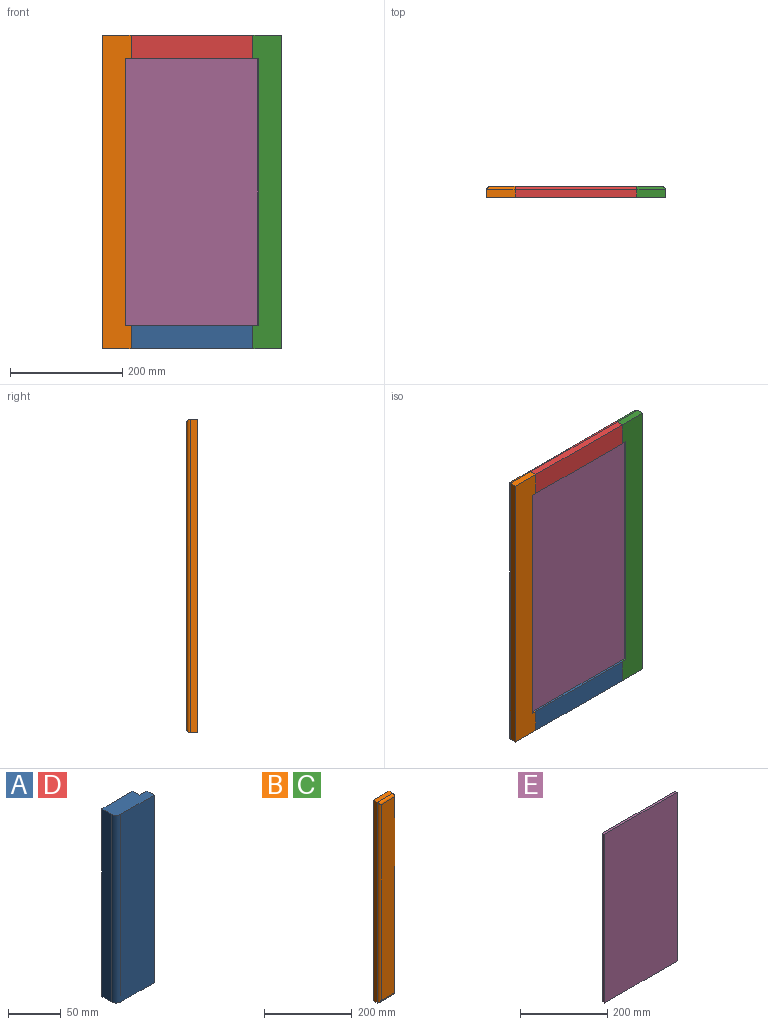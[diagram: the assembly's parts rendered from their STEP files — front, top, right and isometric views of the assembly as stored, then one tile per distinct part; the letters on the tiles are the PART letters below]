
ASSEMBLY  parts=5 mates=4
PART A: 9 faces, bbox 50.8x19.1x217.5 mm
  f0: plane 50.8x19.05mm, normal (0,0,1), area 868.4mm2, adj f2,f3,f4,f5,f6,f7,f8
  f1: plane 50.8x19.05mm, normal (0,0,-1), area 868.4mm2, adj f2,f3,f4,f5,f6,f7,f8
  f2: plane 217.49x12.7mm, normal (-1,0,0), area 2762.1mm2, adj f0,f1,f5,f6
  f3: plane 217.49x44.45mm, normal (0,-1,0), area 9667.3mm2, adj f0,f1,f4,f6
  f4: plane 217.49x9.53mm, normal (1,0,0), area 2071.6mm2, adj f0,f1,f3,f7
  f5: plane 217.49x41.28mm, normal (0,1,0), area 8976.8mm2, adj f0,f1,f2,f8
  f6: cylinder r=6.35mm len=217.49mm, axis (0,0,1), area 2169.3mm2, adj f0,f1,f2,f3
  f7: plane 217.49x9.53mm, normal (0,1,0), area 2071.6mm2, adj f0,f1,f4,f8
  f8: plane 217.49x9.53mm, normal (1,0,0), area 2071.6mm2, adj f0,f1,f5,f7
PART B: 13 faces, bbox 50.8x19.1x558.8 mm
  f0: plane 558.8x19.05mm, normal (1,0,0), area 6091.6mm2, adj f1,f3,f4,f5,f6,f7,f9,f10
  f1: plane 558.8x50.8mm, normal (0,1,0), area 23850.8mm2, adj f0,f2,f4,f5,f9,f10,f11
  f2: plane 558.8x12.7mm, normal (-1,0,0), area 7096.8mm2, adj f1,f4,f5,f8
  f3: plane 546.1x44.45mm, normal (0,-1,0), area 24274.1mm2, adj f0,f6,f7,f8
  f4: plane 50.8x12.7mm, normal (0,0,1), area 645.2mm2, adj f0,f1,f2,f6
  f5: plane 50.8x12.7mm, normal (0,0,-1), area 645.2mm2, adj f0,f1,f2,f7
  f6: cylinder r=6.35mm len=50.8mm, axis (-1,0,0), area 483.7mm2, adj f0,f3,f4,f8
  f7: cylinder r=6.35mm len=50.8mm, axis (1,0,0), area 483.7mm2, adj f0,f3,f5,f8
  f8: cylinder r=6.35mm len=558.8mm, axis (0,0,1), area 5527.8mm2, adj f2,f3,f6,f7
  f9: plane 9.53x9.53mm, normal (0,0,1), area 90.7mm2, adj f0,f1,f11,f12
  f10: plane 9.53x9.53mm, normal (0,0,-1), area 90.7mm2, adj f0,f1,f11,f12
  f11: plane 476.25x9.53mm, normal (1,0,0), area 4536.3mm2, adj f1,f9,f10,f12
  f12: plane 476.25x9.53mm, normal (0,1,0), area 4536.3mm2, adj f0,f9,f10,f11
PART C: same geometry as B
PART D: same geometry as A
PART E: 6 faces, bbox 236.5x6.4x474.7 mm
  f0: plane 474.66x6.35mm, normal (-1,0,0), area 3014.1mm2, adj f1,f3,f4,f5
  f1: plane 236.54x6.35mm, normal (0,0,-1), area 1502mm2, adj f0,f2,f4,f5
  f2: plane 474.66x6.35mm, normal (1,0,0), area 3014.1mm2, adj f1,f3,f4,f5
  f3: plane 236.54x6.35mm, normal (0,0,1), area 1502mm2, adj f0,f2,f4,f5
  f4: plane 474.66x236.54mm, normal (0,-1,0), area 112275.5mm2, adj f0,f1,f2,f3
  f5: plane 474.66x236.54mm, normal (0,1,0), area 112275.5mm2, adj f0,f1,f2,f3
PLACE A rot(axis=(-0.71,0,-0.71),180deg) t=(-239.71,0,-279.4)mm
PLACE B rot(axis=(-1,0,0),180deg) t=(-290.51,0,279.4)mm
PLACE C rot(axis=(0,0,1),180deg) t=(28.58,0,-279.4)mm
PLACE D rot(axis=(-0.71,0,0.71),180deg) t=(-22.23,0,279.4)mm
PLACE E rot(axis=(0,0,1),180deg) t=(-13.49,-15.88,-237.33)mm
MATE fastened C.f4 <-> D.f2  axis (0,0,1) through (-22.23,-12.7,279.4)mm
MATE fastened D.f0 <-> B.f0  axis (-1,0,0) through (-239.71,-19.05,279.4)mm
MATE fastened B.f0 <-> A.f1  axis (1,0,0) through (-239.71,-19.05,-279.4)mm
MATE fastened E.f4 <-> C.f12  axis (0,1,0) through (-13.49,-9.53,237.33)mm
